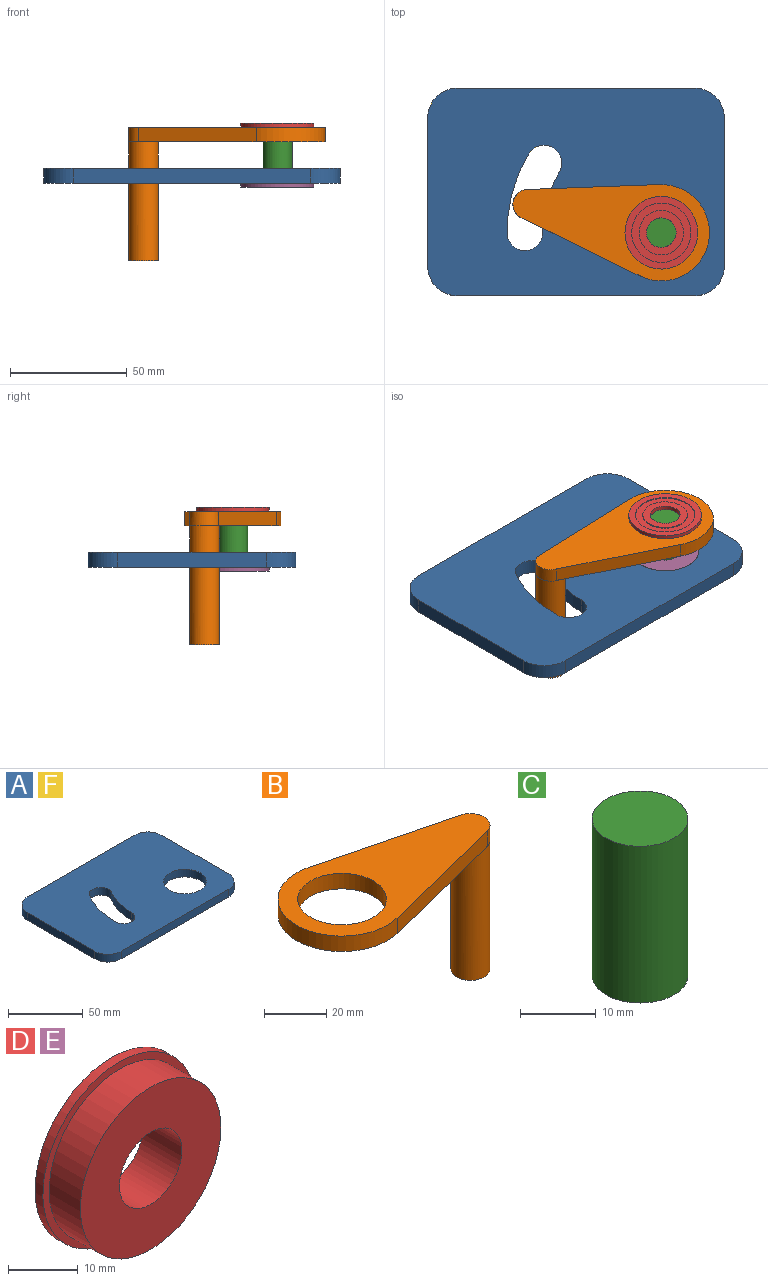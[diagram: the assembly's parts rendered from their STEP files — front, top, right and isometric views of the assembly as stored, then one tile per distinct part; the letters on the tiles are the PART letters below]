
ASSEMBLY  parts=6 mates=4
PART A: 15 faces, bbox 127x88.9x6.4 mm
  f0: plane 101.6x6.35mm, normal (0,1,0), area 645.2mm2, adj f9,f10,f12,f14
  f1: plane 63.5x6.35mm, normal (-1,0,0), area 403.2mm2, adj f9,f10,f12,f13
  f2: plane 101.6x6.35mm, normal (0,-1,0), area 645.2mm2, adj f3,f9,f10,f13
  f3: cylinder r=12.7mm len=12.7mm, axis (0,0,-1), area 126.7mm2, adj f2,f8,f9,f10
  f4: cylinder r=7.62mm len=15.24mm, axis (0,0,-1), area 152mm2, adj f5,f7,f9,f10
  f5: cylinder r=66.04mm len=33.7mm, axis (0,0,-1), area 224.6mm2, adj f4,f6,f9,f10
  f6: cylinder r=7.64mm len=14.21mm, axis (0,0,-1), area 148.1mm2, adj f5,f7,f9,f10
  f7: cylinder r=50.8mm len=26.5mm, axis (0,0,-1), area 177mm2, adj f4,f6,f9,f10
  f8: plane 63.5x6.35mm, normal (1,0,0), area 403.2mm2, adj f3,f9,f10,f14
  f9: plane 127x88.9mm, normal (0,0,1), area 9850.9mm2, adj f0,f1,f2,f3,f4,f5,f6,f7
  f10: plane 127x88.9mm, normal (0,0,-1), area 9850.9mm2, adj f0,f1,f2,f3,f4,f5,f6,f7
  f11: cylinder r=14.29mm len=28.58mm, axis (0,0,-1), area 570mm2, adj f9,f10
  f12: cylinder r=12.7mm len=12.7mm, axis (0,0,1), area 126.7mm2, adj f0,f1,f9,f10
  f13: cylinder r=12.7mm len=12.7mm, axis (0,0,-1), area 126.7mm2, adj f1,f2,f9,f10
  f14: cylinder r=12.7mm len=12.7mm, axis (0,0,-1), area 126.7mm2, adj f0,f8,f9,f10
PART B: 10 faces, bbox 85.4x41.3x56.9 mm
  f0: plane 54.33x13.73mm, normal (0.25,0.97,0), area 341.6mm2, adj f1,f3,f4,f5
  f1: cylinder r=20.64mm len=41.28mm, axis (0,0,-1), area 457.5mm2, adj f0,f2,f4,f5
  f2: plane 54.92x13.85mm, normal (0.24,-0.97,0), area 345.3mm2, adj f1,f3,f4,f5
  f3: cylinder r=6.35mm len=12.43mm, axis (0,0,-1), area 106.1mm2, adj f0,f2,f4,f5,f9
  f4: plane 85.41x41.28mm, normal (0,0,1), area 1714.2mm2, adj f0,f1,f2,f3,f6
  f5: plane 85.4x41.28mm, normal (0,0,-1), area 1590.5mm2, adj f0,f1,f2,f3,f6,f7
  f6: cylinder r=14.29mm len=28.58mm, axis (0,0,-1), area 547.2mm2, adj f4,f5
  f7: cylinder r=6.28mm len=50.8mm, axis (0,0,1), area 2003.4mm2, adj f5,f8,f9
  f8: plane 12.55x12.55mm, normal (0,0,-1), area 123.8mm2, adj f7
  f9: plane 5.04x2.13mm, normal (0,0,1), area 0mm2, adj f3,f7
PART C: 3 faces, bbox 12.7x12.7x25.4 mm
  f0: cylinder r=6.35mm len=25.4mm, axis (0,0,-1), area 1013.4mm2, adj f1,f2
  f1: plane 12.7x12.7mm, normal (0,0,1), area 126.7mm2, adj f0
  f2: plane 12.7x12.7mm, normal (0,0,-1), area 126.7mm2, adj f0
PART D: 10 faces, bbox 31.1x7.9x31.1 mm
  f0: cylinder r=12.7mm len=25.4mm, axis (0,1,0), area 30.4mm2, adj f8,f9
  f1: cylinder r=15.56mm len=31.12mm, axis (0,1,0), area 155.2mm2, adj f7,f8
  f2: cylinder r=14.29mm len=28.58mm, axis (0,1,0), area 570mm2, adj f6,f7
  f3: cylinder r=6.35mm len=12.7mm, axis (0,1,0), area 316.7mm2, adj f5,f6
  f4: cylinder r=9.53mm len=19.05mm, axis (0,1,0), area 22.8mm2, adj f5,f9
  f5: plane 19.05x19.05mm, normal (0,1,0), area 158.3mm2, adj f3,f4
  f6: plane 28.58x28.58mm, normal (0,-1,0), area 514.6mm2, adj f2,f3
  f7: plane 31.12x31.12mm, normal (0,-1,0), area 119.1mm2, adj f1,f2
  f8: plane 31.12x31.12mm, normal (0,1,0), area 253.7mm2, adj f0,f1
  f9: plane 25.4x25.4mm, normal (0,1,0), area 221.7mm2, adj f0,f4
PART E: same geometry as D
PART F: same geometry as A
PLACE A t=(-8.16,1.63,-3.17)mm fixed
PLACE B rot(axis=(0,0,1),168deg) t=(19.55,-35.22,14.54)mm
PLACE C t=(19.55,-35.22,-4.76)mm
PLACE D rot(axis=(0.99,-0.1,-0.1),90.6deg) t=(19.55,-35.22,14.54)mm
PLACE E rot(axis=(-1,0,0),90deg) t=(19.55,-35.22,3.18)mm
PLACE F t=(-8.16,1.63,-3.17)mm
MATE fastened D.f0 <-> B.f1  axis (0,0,1) through (19.55,-35.22,14.54)mm
MATE fastened A.f5 <-> E.f0  axis (0,0,1) through (19.55,-35.22,3.18)mm
MATE fastened C.f0 <-> E.f0  axis (0,0,-1) through (19.55,-35.22,-4.76)mm
MATE revolute C.f0 <-> B.f1  axis (0,0,1) through (19.55,-35.22,20.64)mm
